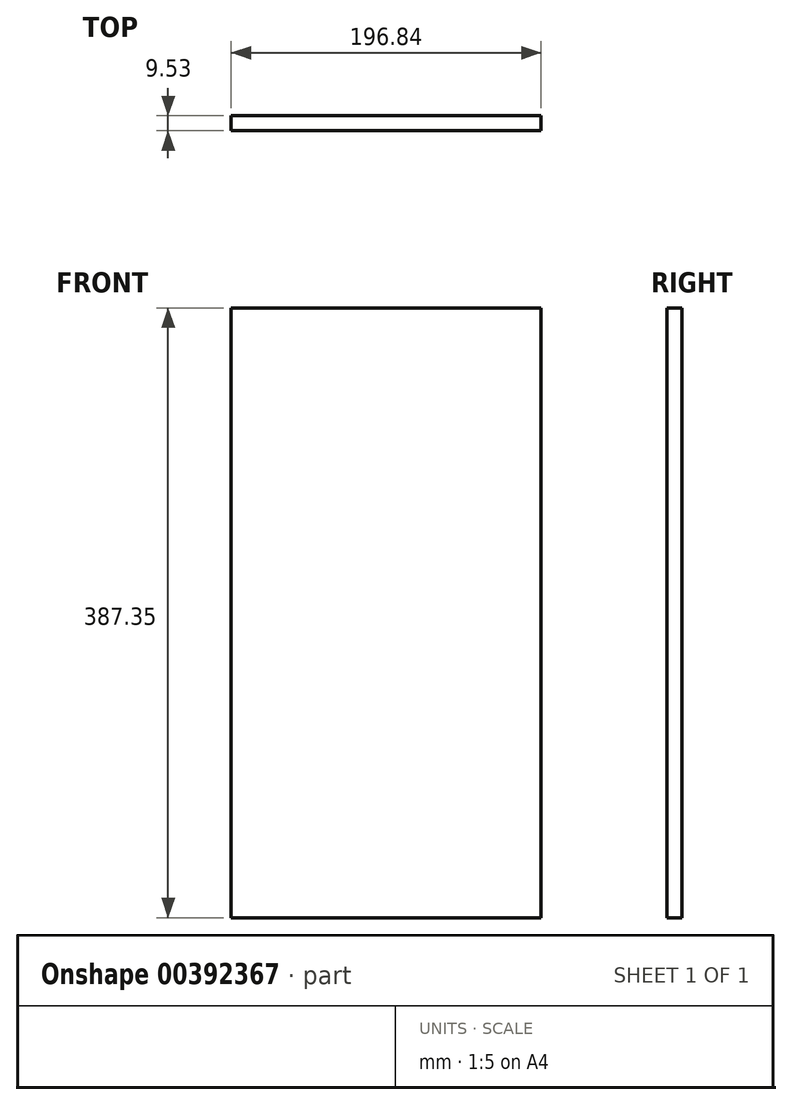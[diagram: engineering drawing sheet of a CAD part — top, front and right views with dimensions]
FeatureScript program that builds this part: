
annotation { "Feature Type Name" : "Feature", "Feature Type Description" : "" }
export const myFeature = defineFeature(function(context is Context, id is Id, definition is map)
    precondition{}
    {
        {
            var Q0;
            Q0=qCreatedBy(makeId("Front.planeOp"),FACE);
            var sketch = newSketch(context, id + "F0", { "sketchPlane" : qUnion([Q0])});
            skLineSegment(sketch, "E0.bottom", {"start": v(-98.42, 0) * mm, "end": v(98.43, 0) * mm});
            skLineSegment(sketch, "E0.top", {"start": v(-98.42, -387.35) * mm, "end": v(98.43, -387.35) * mm});
            skLineSegment(sketch, "E0.left", {"start": v(-98.42, 0) * mm, "end": v(-98.42, -387.35) * mm});
            skLineSegment(sketch, "E0.right", {"start": v(98.43, 0) * mm, "end": v(98.43, -387.35) * mm});
            skSolve(sketch);
        }
        {
            var Q0;
            Q0=makeQuery(id+"F0.imprint","IMPRINT",FACE,{"disambiguationData":[TD([[makeQuery(id+"F0.imprint","IMPRINT",EDGE,{"derivedFrom":sQuery(id+"F0.wireOp",EDGE,"E0.bottom")}),-1.0]])]});
            extrude(context, id + "F1", {"entities" : qUnion([Q0]), "depth" : 9.52 * mm});
        }
    });
